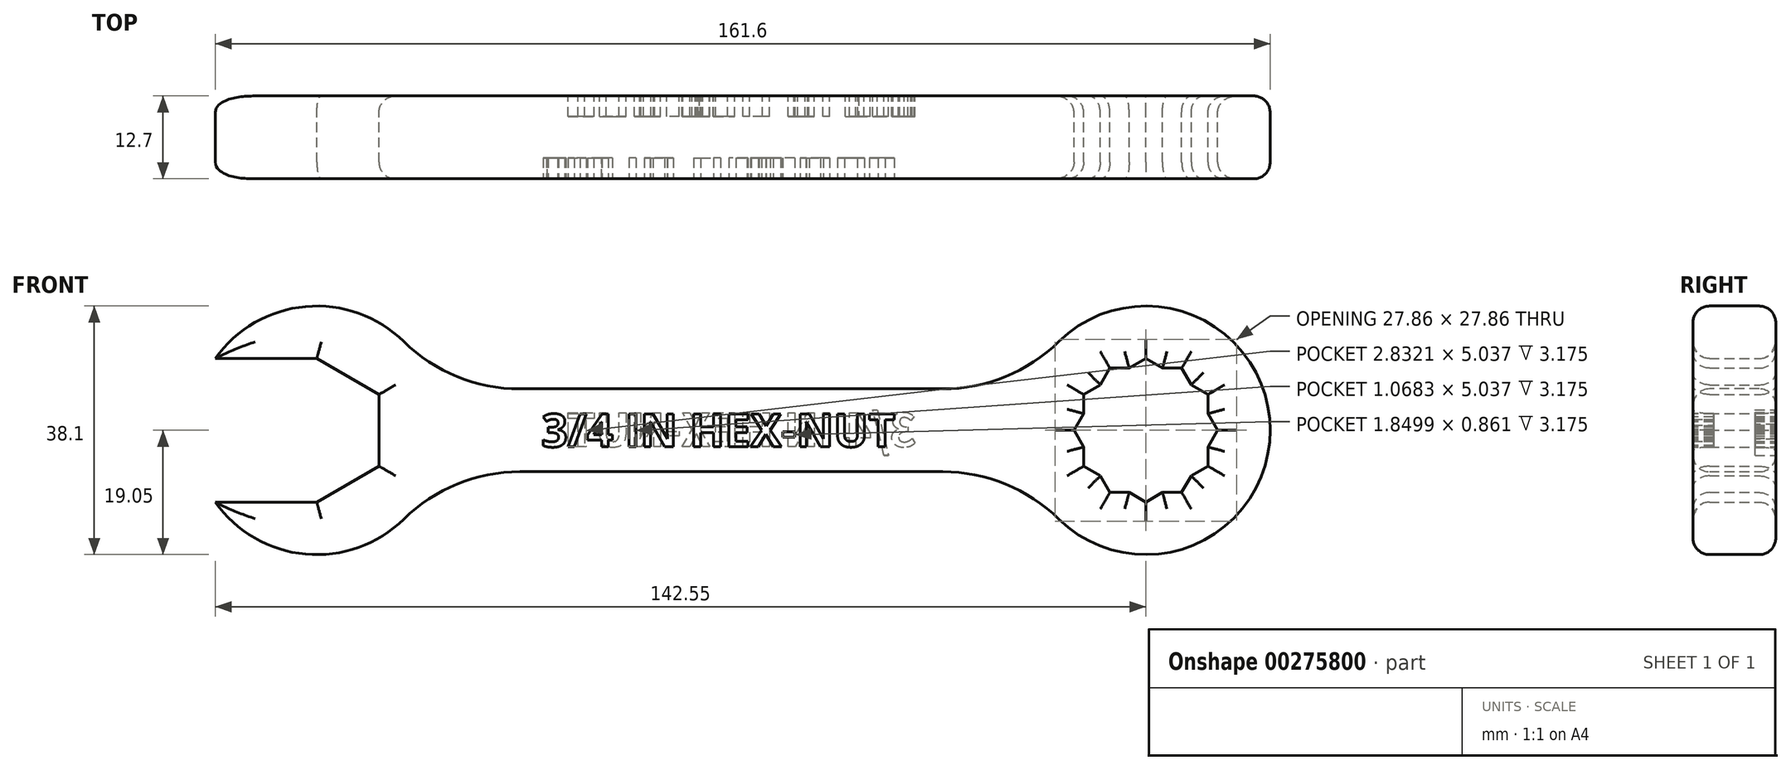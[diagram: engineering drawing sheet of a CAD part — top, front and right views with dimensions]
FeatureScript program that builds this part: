
annotation { "Feature Type Name" : "Feature", "Feature Type Description" : "" }
export const myFeature = defineFeature(function(context is Context, id is Id, definition is map)
    precondition{}
    {
        {
            var Q0;
            Q0=qCreatedBy(makeId("Front.planeOp"),FACE);
            var sketch = newSketch(context, id + "F0", { "sketchPlane" : qUnion([Q0])});
            skLineSegment(sketch, "E0.bottom", {"start": v(56.4, 6.35) * mm, "end": v(-55.45, 6.35) * mm});
            skLineSegment(sketch, "E0.top", {"start": v(56.4, -6.35) * mm, "end": v(-55.45, -6.35) * mm});
            skPoint(sketch, "E0.middle", {"position": v(0, 0) * mm});
            skArc(sketch, "E1", {"start": v(-79.05, -11) * mm, "mid": v(-44.45, 0) * mm, "end": v(-79.05, 11) * mm});
            skCircle(sketch, "E2", {"center": v(63.5, 0) * mm, "radius": 19.05 * mm});
            skLineSegment(sketch, "E3.0", {"start": v(-53.97, 5.5) * mm, "end": v(-53.97, -5.5) * mm});
            skLineSegment(sketch, "E3.1", {"start": v(-53.97, -5.5) * mm, "end": v(-63.5, -11) * mm});
            skLineSegment(sketch, "E3.5", {"start": v(-63.5, 11) * mm, "end": v(-53.97, 5.5) * mm});
            skPoint(sketch, "E3.0.midPoint", {"position": v(-53.97, 0) * mm});
            skLineSegment(sketch, "E4", {"start": v(-63.5, 11) * mm, "end": v(-79.05, 11) * mm});
            skLineSegment(sketch, "E5", {"start": v(-63.5, -11) * mm, "end": v(-79.05, -11) * mm});
            skPoint(sketch, "E6.orphan", {"position": v(-73.03, 5.5) * mm});
            skPoint(sketch, "E7.orphan", {"position": v(-63.5, -6.35) * mm});
            skPoint(sketch, "E8.orphan", {"position": v(-63.5, 6.35) * mm});
            skCircle(sketch, "E9.cCircle", {"center": v(63.5, 0) * mm, "radius": 9.53 * mm, "construction": true});
            skLineSegment(sketch, "E9.0", {"start": v(69, -9.52) * mm, "end": v(58, -9.53) * mm});
            skLineSegment(sketch, "E9.1", {"start": v(58, -9.52) * mm, "end": v(52.5, 0) * mm});
            skLineSegment(sketch, "E9.2", {"start": v(52.5, 0) * mm, "end": v(58, 9.52) * mm});
            skLineSegment(sketch, "E9.3", {"start": v(58, 9.52) * mm, "end": v(69, 9.53) * mm});
            skLineSegment(sketch, "E9.4", {"start": v(69, 9.53) * mm, "end": v(74.5, 0) * mm});
            skLineSegment(sketch, "E9.5", {"start": v(74.5, 0) * mm, "end": v(69, -9.53) * mm});
            skPoint(sketch, "E9.0.midPoint", {"position": v(63.5, -9.53) * mm});
            skPoint(sketch, "E10.orphan", {"position": v(63.5, -6.35) * mm});
            skPoint(sketch, "E0.left.start.orphan", {"position": v(63.5, 6.35) * mm});
            skLineSegment(sketch, "E11.0", {"start": v(73.03, 5.5) * mm, "end": v(73.03, -5.5) * mm});
            skLineSegment(sketch, "E11.1", {"start": v(73.03, -5.5) * mm, "end": v(63.5, -11) * mm});
            skLineSegment(sketch, "E11.2", {"start": v(63.5, -11) * mm, "end": v(53.97, -5.5) * mm});
            skLineSegment(sketch, "E11.3", {"start": v(53.97, -5.5) * mm, "end": v(53.97, 5.5) * mm});
            skLineSegment(sketch, "E11.4", {"start": v(53.97, 5.5) * mm, "end": v(63.5, 11) * mm});
            skLineSegment(sketch, "E11.5", {"start": v(63.5, 11) * mm, "end": v(73.03, 5.5) * mm});
            skPoint(sketch, "E11.0.midPoint", {"position": v(73.03, 0) * mm});
            skSolve(sketch);
        }
        {
            var Q0;
            Q0 = qSketchRegion(id + "F0", true);
            extrude(context, id + "F1", {"entities" : qUnion([Q0]), "depth" : 12.7 * mm});
        }
        {
            var Q0;
            Q0=makeQuery(id+"F1.opExtrude","SWEPT_EDGE",EDGE,{"disambiguationData":[OSD([sQuery(id+"F0.wireOp",EDGE,"E0.bottom"),sQuery(id+"F0.wireOp",EDGE,"E1")])]});
            var Q1;
            Q1=makeQuery(id+"F1.opExtrude","SWEPT_EDGE",EDGE,{"disambiguationData":[OSD([sQuery(id+"F0.wireOp",EDGE,"E0.bottom"),sQuery(id+"F0.wireOp",EDGE,"E2")])]});
            var Q2;
            Q2=makeQuery(id+"F1.opExtrude","SWEPT_EDGE",EDGE,{"disambiguationData":[OSD([sQuery(id+"F0.wireOp",EDGE,"E0.top"),sQuery(id+"F0.wireOp",EDGE,"E2")])]});
            var Q3;
            Q3=makeQuery(id+"F1.opExtrude","SWEPT_EDGE",EDGE,{"disambiguationData":[OSD([sQuery(id+"F0.wireOp",EDGE,"E0.top"),sQuery(id+"F0.wireOp",EDGE,"E1")])]});
            fillet(context, id + "F2", {"entities" : qUnion([Q0, Q1, Q2, Q3]), "radius" : 25.4 * mm, "tangentPropagation" : true, "allowEdgeOverflow" : false});
        }
        {
            var Q0;
            Q0=makeQuery(id+"F1.opExtrude","CAP_FACE",FACE,{"disambiguationData":[OSD([sQuery(id+"F0.wireOp",EDGE,"E0.bottom"),sQuery(id+"F0.wireOp",EDGE,"E0.top"),sQuery(id+"F0.wireOp",EDGE,"E1"),sQuery(id+"F0.wireOp",EDGE,"E2"),sQuery(id+"F0.wireOp",EDGE,"E3.0"),sQuery(id+"F0.wireOp",EDGE,"E3.1"),sQuery(id+"F0.wireOp",EDGE,"E3.5"),sQuery(id+"F0.wireOp",EDGE,"E4"),sQuery(id+"F0.wireOp",EDGE,"E5"),sQuery(id+"F0.wireOp",EDGE,"E9.0"),sQuery(id+"F0.wireOp",EDGE,"E9.1"),sQuery(id+"F0.wireOp",EDGE,"E9.2"),sQuery(id+"F0.wireOp",EDGE,"E9.3"),sQuery(id+"F0.wireOp",EDGE,"E9.4"),sQuery(id+"F0.wireOp",EDGE,"E9.5")])],"isStart":true});
            var Q1;
            Q1=makeQuery(id+"F1.opExtrude","CAP_FACE",FACE,{"disambiguationData":[OSD([sQuery(id+"F0.wireOp",EDGE,"E0.bottom"),sQuery(id+"F0.wireOp",EDGE,"E0.top"),sQuery(id+"F0.wireOp",EDGE,"E1"),sQuery(id+"F0.wireOp",EDGE,"E2"),sQuery(id+"F0.wireOp",EDGE,"E3.0"),sQuery(id+"F0.wireOp",EDGE,"E3.1"),sQuery(id+"F0.wireOp",EDGE,"E3.5"),sQuery(id+"F0.wireOp",EDGE,"E4"),sQuery(id+"F0.wireOp",EDGE,"E5"),sQuery(id+"F0.wireOp",EDGE,"E9.0"),sQuery(id+"F0.wireOp",EDGE,"E9.1"),sQuery(id+"F0.wireOp",EDGE,"E9.2"),sQuery(id+"F0.wireOp",EDGE,"E9.3"),sQuery(id+"F0.wireOp",EDGE,"E9.4"),sQuery(id+"F0.wireOp",EDGE,"E9.5")])],"isStart":false});
            fillet(context, id + "F3", {"entities" : qUnion([Q0, Q1]), "radius" : 2.54 * mm, "tangentPropagation" : true, "allowEdgeOverflow" : false});
        }
        {
            var Q0;
            Q0=makeQuery(id+"F1.opExtrude","CAP_FACE",FACE,{"disambiguationData":[OSD([sQuery(id+"F0.wireOp",EDGE,"E0.bottom"),sQuery(id+"F0.wireOp",EDGE,"E0.top"),sQuery(id+"F0.wireOp",EDGE,"E1"),sQuery(id+"F0.wireOp",EDGE,"E2"),sQuery(id+"F0.wireOp",EDGE,"E3.0"),sQuery(id+"F0.wireOp",EDGE,"E3.1"),sQuery(id+"F0.wireOp",EDGE,"E3.5"),sQuery(id+"F0.wireOp",EDGE,"E4"),sQuery(id+"F0.wireOp",EDGE,"E5"),sQuery(id+"F0.wireOp",EDGE,"E9.0"),sQuery(id+"F0.wireOp",EDGE,"E9.1"),sQuery(id+"F0.wireOp",EDGE,"E9.2"),sQuery(id+"F0.wireOp",EDGE,"E9.3"),sQuery(id+"F0.wireOp",EDGE,"E9.4"),sQuery(id+"F0.wireOp",EDGE,"E9.5")])],"isStart":true});
            var sketch = newSketch(context, id + "F4", { "sketchPlane" : qUnion([Q0])});
            skText(sketch, "E12", { "text": "3/4 IN HEX-NUT", "fontName": "NotoSansCJKsc-Bold.otf"});
            const initialGuessF4  = {"E12": [-0.02835, -0.00254, 1, 0, 0.00508]};
            skSetInitialGuess(sketch, initialGuessF4);
            skSolve(sketch);
        }
        {
            var Q0;
            Q0 = qSketchRegion(id + "F4", true);
            extrude(context, id + "F5", {"entities" : qUnion([Q0]), "operationType" : NewBodyOperationType.REMOVE, "oppositeDirection" : true, "depth" : 3.17 * mm});
        }
        {
            var Q0;
            Q0=makeQuery(id+"F1.opExtrude","CAP_FACE",FACE,{"disambiguationData":[OSD([sQuery(id+"F0.wireOp",EDGE,"E0.bottom"),sQuery(id+"F0.wireOp",EDGE,"E0.top"),sQuery(id+"F0.wireOp",EDGE,"E1"),sQuery(id+"F0.wireOp",EDGE,"E2"),sQuery(id+"F0.wireOp",EDGE,"E3.0"),sQuery(id+"F0.wireOp",EDGE,"E3.1"),sQuery(id+"F0.wireOp",EDGE,"E3.5"),sQuery(id+"F0.wireOp",EDGE,"E4"),sQuery(id+"F0.wireOp",EDGE,"E5"),sQuery(id+"F0.wireOp",EDGE,"E9.0"),sQuery(id+"F0.wireOp",EDGE,"E9.1"),sQuery(id+"F0.wireOp",EDGE,"E9.2"),sQuery(id+"F0.wireOp",EDGE,"E9.3"),sQuery(id+"F0.wireOp",EDGE,"E9.4"),sQuery(id+"F0.wireOp",EDGE,"E9.5")])],"isStart":false});
            var sketch = newSketch(context, id + "F6", { "sketchPlane" : qUnion([Q0])});
            skText(sketch, "E13", { "text": "3/4 IN HEX-NUT", "fontName": "OpenSans-Bold.ttf"});
            const initialGuessF6  = {"E13": [-0.0291, -0.00254, 1, 0, 0.00508]};
            skSetInitialGuess(sketch, initialGuessF6);
            skSolve(sketch);
        }
        {
            var Q0;
            Q0 = qSketchRegion(id + "F6", true);
            extrude(context, id + "F7", {"entities" : qUnion([Q0]), "operationType" : NewBodyOperationType.REMOVE, "oppositeDirection" : true, "depth" : 3.17 * mm});
        }
    });
